# Revit family: РОСМА_ТермометрКоррозионностойкий(УниверсПрисоед)
name_source: partatom
category: Арматура трубопроводов
revit_build: Autodesk Revit 2018 (Build: 20180423_1000(x64)
units: mm (PartAtom-declared; Revit-internal decimal feet)

## family parameters
Всегда вертикально = Да
На основе рабочей плоскости = Нет
Общий = Нет
При загрузке вырезать с полостями = Нет
Размер круглого соединителя = Использовать диаметр
Тип детали = Вставляется

## types (3) — shared parameters
ADSK_Единица измерения = шт.
ADSK_Количество = 1
DN = 15.00 мм
Table = спец_коррозионностойкий (универсальное присоединение)
Table_2 = размеры_коррозионностойкий (универсальное присоединение)
URL = https://rosma.spb.ru
Группа модели = Оборудование
Длина01 = ᅠ : 46мм
Длина02 = ᅠ : 64мм
Длина03 = ᅠ : 100мм
Длина04 = ᅠ : 150мм
Длина05 = ᅠ : 200мм
Длина06 = ᅠ : 250мм
Длина07 = ᅠ : 300мм
Изготовитель = ЗАО "РОСМА"
Класс точности = 1,5
Климатическое исполнение = Группа Д2 по ГОСТ Р 52931; климатическое исполнение УХЛ категории 1.1 по ГОСТ 15150
Код IP = IP54
Межповерочный интервал = 3 года
Описание = Тип БТ, серия 220. Коррозионностойкий термометр с универсальным присоединением (поворотно-откидным корпусом) с резьбой на штоке. Предназначен для измерения температуры агрессивных жидкостей и газов.
Температура01 = ‎ : -30...+50°С
Температура02 = ‎ : 0...+60°С
Температура03 = ‎ : 0...+100°С
Температура04 = ‎ : 0...+120°С
Температура05 = ‎ : 0...+160°С
Температура06 = ‎ : 0...+250°С
Температура07 = ‎ : 0...+300°С
Температура08 = ‎ : 0...+350°С
Температура09 = ‎ : 0...+450°С
Техническая документация = ТУ 4211-001-4719015564-2008
лого_задн_стенка = Нет

## per-type parameters (varying)
| type | h_зоныОбсл | а_зоныОбсл |
| 44 | 152 мм | 107 мм |
| 54 | 152 мм | 107 мм |
| 74 | 80 мм | 160 мм |

note: column(s) folded — value = type name in every type: Исполнение
